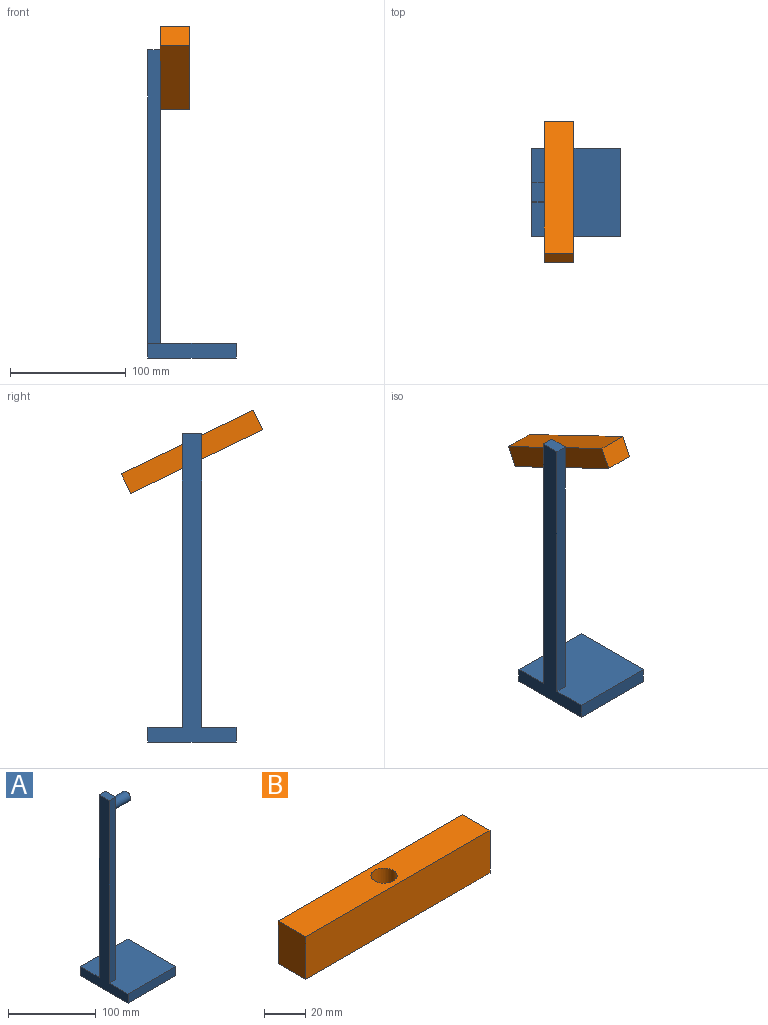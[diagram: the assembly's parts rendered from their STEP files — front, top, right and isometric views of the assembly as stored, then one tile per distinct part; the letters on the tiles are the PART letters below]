
ASSEMBLY  parts=2 mates=1
PART A: 12 faces, bbox 76.2x76.2x266.7 mm
  f0: plane 266.7x76.2mm, normal (-1,0,0), area 5200mm2, adj f1,f3,f4,f5,f7,f8,f9
  f1: plane 76.2x12.7mm, normal (0,-1,0), area 967.7mm2, adj f0,f2,f4,f5
  f2: plane 76.2x12.7mm, normal (1,0,0), area 967.7mm2, adj f1,f3,f4,f5
  f3: plane 76.2x12.7mm, normal (0,1,0), area 967.7mm2, adj f0,f2,f4,f5
  f4: plane 76.2x76.2mm, normal (0,0,1), area 5633.1mm2, adj f0,f1,f2,f3,f6,f7,f8
  f5: plane 76.2x76.2mm, normal (0,0,-1), area 5806.4mm2, adj f0,f1,f2,f3
  f6: plane 254x16.66mm, normal (1,0,0), area 4105.6mm2, adj f4,f7,f8,f9,f10
  f7: plane 254x10.4mm, normal (0,1,0), area 2642.7mm2, adj f0,f4,f6,f9
  f8: plane 254x10.4mm, normal (0,-1,0), area 2642.7mm2, adj f0,f4,f6,f9
  f9: plane 16.66x10.4mm, normal (0,0,1), area 173.4mm2, adj f0,f6,f7,f8
  f10: cylinder r=6.35mm len=25.4mm, axis (-1,0,0), area 1013.4mm2, adj f6,f11
  f11: plane 12.7x12.7mm, normal (1,0,0), area 126.7mm2, adj f10
PART B: 7 faces, bbox 127x19.1x25.4 mm
  f0: plane 25.4x19.05mm, normal (1,0,0), area 483.9mm2, adj f1,f3,f5,f6
  f1: plane 127x25.4mm, normal (0,1,0), area 3225.8mm2, adj f0,f2,f5,f6
  f2: plane 25.4x19.05mm, normal (-1,0,0), area 483.9mm2, adj f1,f3,f5,f6
  f3: plane 127x25.4mm, normal (0,-1,0), area 3225.8mm2, adj f0,f2,f5,f6
  f4: cylinder r=6.36mm len=25.4mm, axis (0,0,-1), area 1015.4mm2, adj f5,f6
  f5: plane 127x19.05mm, normal (0,0,1), area 2292.2mm2, adj f0,f1,f2,f3,f4
  f6: plane 127x19.05mm, normal (0,0,-1), area 2292.2mm2, adj f0,f1,f2,f3,f4
PLACE A t=(-112.82,-48.2,-83.79)mm fixed
PLACE B rot(axis=(-0.65,0.41,-0.65),135.8deg) t=(-102.41,-10.1,167.45)mm
MATE revolute B.f4 <-> A.f10  axis (1,0,0) through (-77.01,-10.1,167.45)mm
